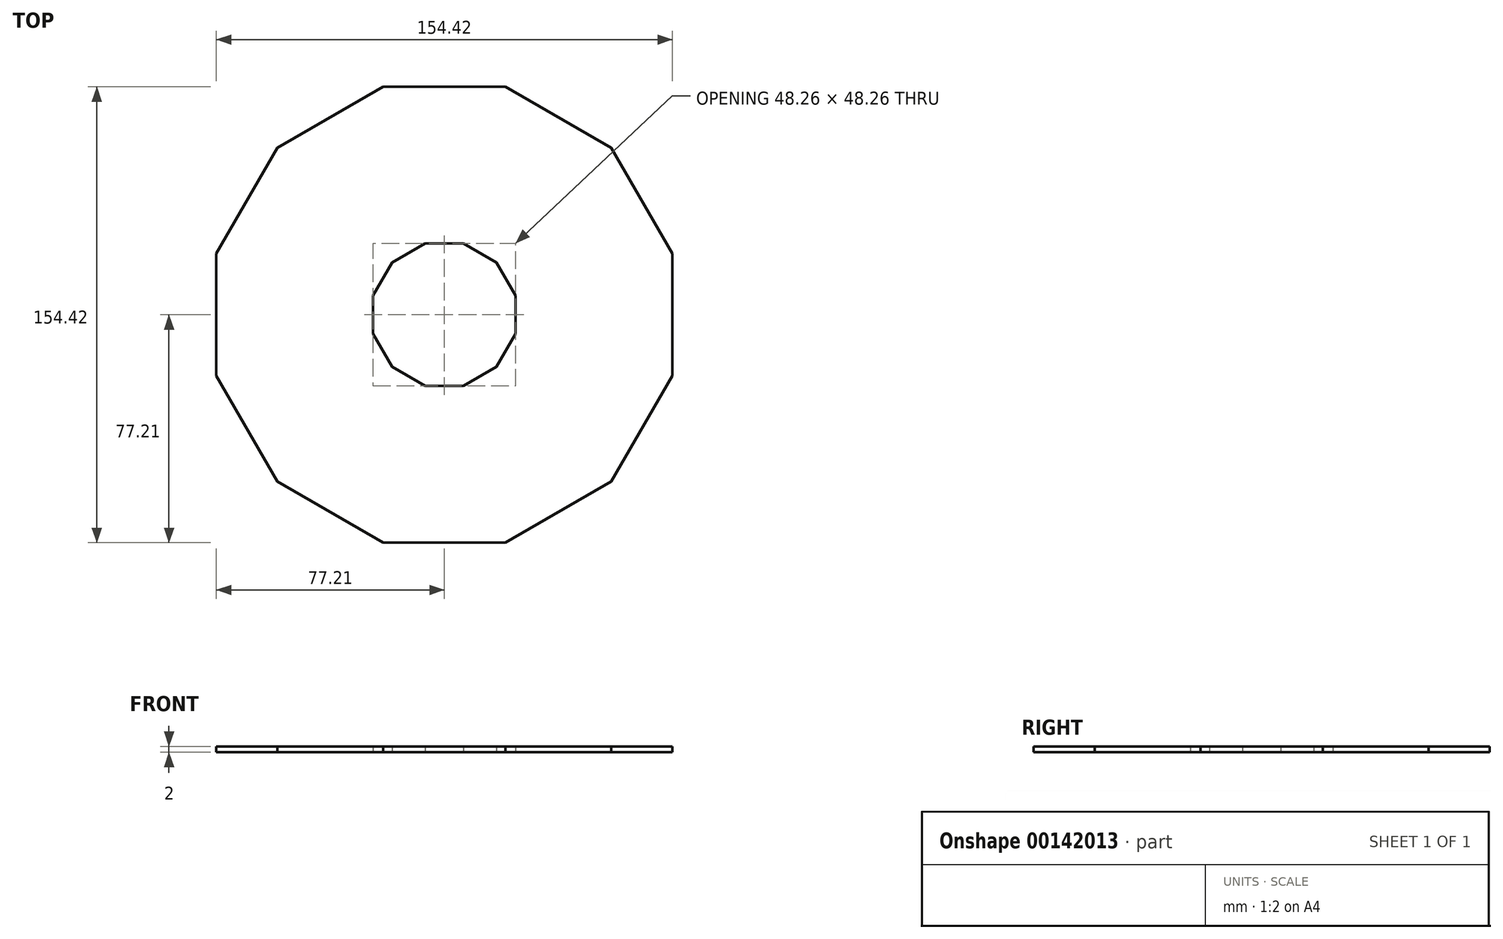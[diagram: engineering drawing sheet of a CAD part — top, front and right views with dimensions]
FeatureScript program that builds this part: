
annotation { "Feature Type Name" : "Feature", "Feature Type Description" : "" }
export const myFeature = defineFeature(function(context is Context, id is Id, definition is map)
    precondition{}
    {
        {
            var Q0;
            Q0=qCreatedBy(makeId("Top.planeOp"),FACE);
            var sketch = newSketch(context, id + "F0", { "sketchPlane" : qUnion([Q0])});
            skCircle(sketch, "E0.cCircle", {"center": v(0, 0) * mm, "radius": 77.2 * mm, "construction": true});
            skLineSegment(sketch, "E0.0", {"start": v(-20.69, 77.2) * mm, "end": v(20.69, 77.2) * mm});
            skLineSegment(sketch, "E0.1", {"start": v(20.69, 77.2) * mm, "end": v(56.52, 56.52) * mm});
            skLineSegment(sketch, "E0.2", {"start": v(56.52, 56.52) * mm, "end": v(77.2, 20.69) * mm});
            skLineSegment(sketch, "E0.3", {"start": v(77.2, 20.69) * mm, "end": v(77.2, -20.69) * mm});
            skLineSegment(sketch, "E0.4", {"start": v(77.2, -20.69) * mm, "end": v(56.52, -56.52) * mm});
            skLineSegment(sketch, "E0.5", {"start": v(56.52, -56.52) * mm, "end": v(20.69, -77.2) * mm});
            skLineSegment(sketch, "E0.6", {"start": v(20.69, -77.2) * mm, "end": v(-20.69, -77.2) * mm});
            skLineSegment(sketch, "E0.7", {"start": v(-20.69, -77.2) * mm, "end": v(-56.52, -56.52) * mm});
            skLineSegment(sketch, "E0.8", {"start": v(-56.52, -56.52) * mm, "end": v(-77.2, -20.69) * mm});
            skLineSegment(sketch, "E0.9", {"start": v(-77.2, -20.69) * mm, "end": v(-77.2, 20.69) * mm});
            skLineSegment(sketch, "E0.10", {"start": v(-77.2, 20.69) * mm, "end": v(-56.52, 56.52) * mm});
            skLineSegment(sketch, "E0.11", {"start": v(-56.52, 56.52) * mm, "end": v(-20.69, 77.2) * mm});
            skPoint(sketch, "E0.0.midPoint", {"position": v(0, 77.2) * mm});
            skCircle(sketch, "E1.cCircle", {"center": v(0, 0) * mm, "radius": 24.13 * mm, "construction": true});
            skLineSegment(sketch, "E1.0", {"start": v(-6.47, 24.13) * mm, "end": v(6.47, 24.13) * mm});
            skLineSegment(sketch, "E1.1", {"start": v(6.47, 24.13) * mm, "end": v(17.66, 17.66) * mm});
            skLineSegment(sketch, "E1.2", {"start": v(17.66, 17.66) * mm, "end": v(24.13, 6.47) * mm});
            skLineSegment(sketch, "E1.3", {"start": v(24.13, 6.47) * mm, "end": v(24.13, -6.47) * mm});
            skLineSegment(sketch, "E1.4", {"start": v(24.13, -6.47) * mm, "end": v(17.66, -17.66) * mm});
            skLineSegment(sketch, "E1.5", {"start": v(17.66, -17.66) * mm, "end": v(6.47, -24.13) * mm});
            skLineSegment(sketch, "E1.6", {"start": v(6.47, -24.13) * mm, "end": v(-6.47, -24.13) * mm});
            skLineSegment(sketch, "E1.7", {"start": v(-6.47, -24.13) * mm, "end": v(-17.66, -17.66) * mm});
            skLineSegment(sketch, "E1.8", {"start": v(-17.66, -17.66) * mm, "end": v(-24.13, -6.47) * mm});
            skLineSegment(sketch, "E1.9", {"start": v(-24.13, -6.47) * mm, "end": v(-24.13, 6.47) * mm});
            skLineSegment(sketch, "E1.10", {"start": v(-24.13, 6.47) * mm, "end": v(-17.66, 17.66) * mm});
            skLineSegment(sketch, "E1.11", {"start": v(-17.66, 17.66) * mm, "end": v(-6.47, 24.13) * mm});
            skPoint(sketch, "E1.0.midPoint", {"position": v(0, 24.13) * mm});
            skSolve(sketch);
        }
        {
            var Q0;
            Q0 = qSketchRegion(id + "F0", true);
            extrude(context, id + "F1", {"entities" : qUnion([Q0]), "depth" : 1.59 * mm});
        }
        {
            var Q0;
            Q0 = qSketchRegion(id + "F0", true);
            extrude(context, id + "F2", {"entities" : qUnion([Q0]), "operationType" : NewBodyOperationType.ADD, "depth" : 2 * mm});
        }
        {
            var Q0;
            Q0=qCreatedBy(makeId("Front.planeOp"),FACE);
            var sketch = newSketch(context, id + "F3", { "sketchPlane" : qUnion([Q0])});
            skLineSegment(sketch, "E2", {"start": v(77.2, 12.75) * mm, "end": v(39.1, 12.75) * mm});
            skLineSegment(sketch, "E3", {"start": v(77.2, 12.75) * mm, "end": v(357.67, 174.67) * mm});
            skSolve(sketch);
        }
        {
            var Q0;
            Q0=qCreatedBy(makeId("Top.planeOp"),FACE);
            var Q1;
            Q1=sQuery(id+"F3.wireOp",VERTEX,"E3.end");
            cPlane(context, id + "F4", {"entities" : qUnion([Q0, Q1]), "cplaneType" : CPlaneType.PLANE_POINT, "offset" : 25.4 * mm, "width" : 152.4 * mm, "height" : 152.4 * mm});
        }
    });
